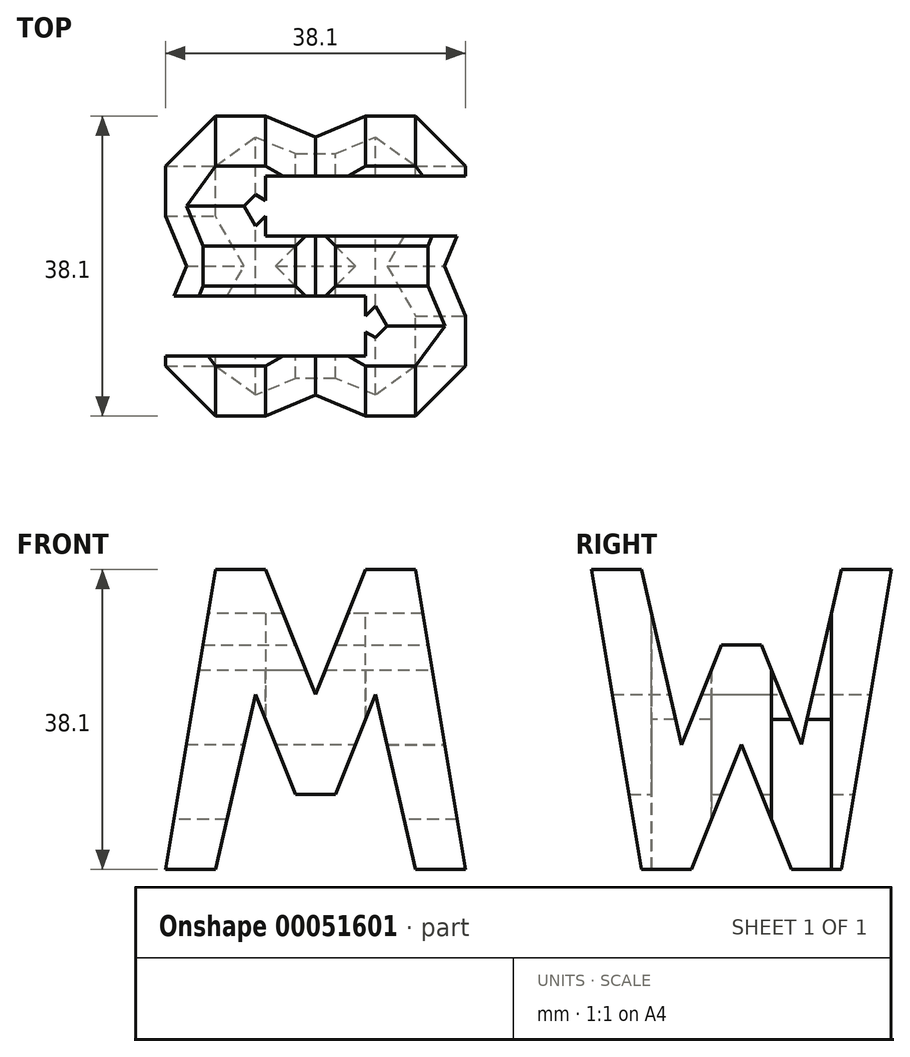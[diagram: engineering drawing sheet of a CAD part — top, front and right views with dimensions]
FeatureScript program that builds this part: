
annotation { "Feature Type Name" : "Feature", "Feature Type Description" : "" }
export const myFeature = defineFeature(function(context is Context, id is Id, definition is map)
    precondition{}
    {
        {
            var Q0;
            Q0=qCreatedBy(makeId("Front.planeOp"),FACE);
            var sketch = newSketch(context, id + "F0", { "sketchPlane" : qUnion([Q0])});
            skLineSegment(sketch, "E0.bottom", {"start": v(-38.1, 38.1) * mm, "end": v(0, 38.1) * mm});
            skLineSegment(sketch, "E0.top", {"start": v(-38.1, 0) * mm, "end": v(0, 0) * mm});
            skLineSegment(sketch, "E0.left", {"start": v(-38.1, 38.1) * mm, "end": v(-38.1, 0) * mm});
            skLineSegment(sketch, "E0.right", {"start": v(0, 38.1) * mm, "end": v(0, 0) * mm});
            skSolve(sketch);
        }
        {
            var Q0;
            Q0=makeQuery(id+"F0.imprint","IMPRINT",FACE,{"disambiguationData":[TD([[makeQuery(id+"F0.imprint","IMPRINT",EDGE,{"derivedFrom":sQuery(id+"F0.wireOp",EDGE,"E0.bottom")}),-1.0]])]});
            extrude(context, id + "F1", {"entities" : qUnion([Q0]), "depth" : 38.1 * mm});
        }
        {
            var Q0;
            Q0=qCreatedBy(makeId("Right.planeOp"),FACE);
            cPlane(context, id + "F2", {"entities" : qUnion([Q0]), "cplaneType" : CPlaneType.OFFSET, "offset" : 0 * mm, "width" : 152.4 * mm, "height" : 152.4 * mm});
        }
        {
            var Q0;
            Q0=qCreatedBy(makeId("Top.planeOp"),FACE);
            cPlane(context, id + "F3", {"entities" : qUnion([Q0]), "cplaneType" : CPlaneType.OFFSET, "offset" : 38.1 * mm, "width" : 152.4 * mm, "height" : 152.4 * mm});
        }
        {
            var Q0;
            Q0=qCreatedBy(id+"F2.planeOp",FACE);
            var sketch = newSketch(context, id + "F4", { "sketchPlane" : qUnion([Q0])});
            skLineSegment(sketch, "E1.bottom", {"start": v(0, 0) * mm, "end": v(-38.1, 0) * mm});
            skLineSegment(sketch, "E1.top", {"start": v(0, 38.1) * mm, "end": v(-38.1, 38.1) * mm});
            skLineSegment(sketch, "E1.left", {"start": v(0, 0) * mm, "end": v(0, 38.1) * mm});
            skLineSegment(sketch, "E1.right", {"start": v(-38.1, 0) * mm, "end": v(-38.1, 38.1) * mm});
            skLineSegment(sketch, "E2", {"start": v(-38.1, 38.1) * mm, "end": v(-31.75, 0) * mm});
            skLineSegment(sketch, "E3", {"start": v(-31.75, 0) * mm, "end": v(-25.4, 0) * mm});
            skLineSegment(sketch, "E4", {"start": v(-25.4, 0) * mm, "end": v(-19.05, 15.88) * mm});
            skLineSegment(sketch, "E5", {"start": v(-19.05, 15.88) * mm, "end": v(-12.7, 0) * mm});
            skLineSegment(sketch, "E6", {"start": v(-12.7, 0) * mm, "end": v(-6.35, 0) * mm});
            skLineSegment(sketch, "E7", {"start": v(-6.35, 0) * mm, "end": v(0, 38.1) * mm});
            skLineSegment(sketch, "E8", {"start": v(-6.35, 38.1) * mm, "end": v(-11.43, 15.87) * mm});
            skLineSegment(sketch, "E9", {"start": v(-21.6, 28.52) * mm, "end": v(-26.67, 15.82) * mm});
            skLineSegment(sketch, "E10", {"start": v(-26.67, 15.82) * mm, "end": v(-31.75, 38.1) * mm});
            skLineSegment(sketch, "E11", {"start": v(-31.75, 38.1) * mm, "end": v(-38.1, 38.1) * mm});
            skLineSegment(sketch, "E12", {"start": v(-21.6, 28.52) * mm, "end": v(-16.51, 28.52) * mm});
            skLineSegment(sketch, "E13", {"start": v(-11.43, 15.87) * mm, "end": v(-16.51, 28.52) * mm});
            skSolve(sketch);
        }
        {
            var Q0;
            {var subQ1=sQuery(id+"F4.wireOp",EDGE,"E8");Q0=makeQuery(id+"F4.imprint","IMPRINT",FACE,{"disambiguationData":[TD([[makeQuery(id+"F4.imprint","IMPRINT",EDGE,{"derivedFrom":subQ1}),-1.0]])]});}
            var Q1;
            {var subQ0=sQuery(id+"F4.wireOp",EDGE,"E1.right");Q1=makeQuery(id+"F4.imprint","IMPRINT",FACE,{"disambiguationData":[TD([[makeQuery(id+"F4.imprint","IMPRINT",EDGE,{"derivedFrom":subQ0}),-1.0]])]});}
            var Q2;
            {var subQ0=sQuery(id+"F4.wireOp",EDGE,"E4");Q2=makeQuery(id+"F4.imprint","IMPRINT",FACE,{"disambiguationData":[TD([[makeQuery(id+"F4.imprint","IMPRINT",EDGE,{"derivedFrom":subQ0}),-1.0]])]});}
            var Q3;
            {var subQ0=sQuery(id+"F4.wireOp",EDGE,"E1.left");Q3=makeQuery(id+"F4.imprint","IMPRINT",FACE,{"disambiguationData":[TD([[makeQuery(id+"F4.imprint","IMPRINT",EDGE,{"derivedFrom":subQ0}),1.0]])]});}
            extrude(context, id + "F5", {"entities" : qUnion([Q0, Q1, Q2, Q3]), "operationType" : NewBodyOperationType.REMOVE, "oppositeDirection" : true, "depth" : 38.1 * mm});
        }
        {
            var Q0;
            Q0=qCreatedBy(makeId("Front.planeOp"),FACE);
            var sketch = newSketch(context, id + "F6", { "sketchPlane" : qUnion([Q0])});
            skLineSegment(sketch, "E14", {"start": v(0, 38.1) * mm, "end": v(-38.1, 38.1) * mm});
            skLineSegment(sketch, "E15", {"start": v(-38.1, 38.1) * mm, "end": v(-38.1, 0) * mm});
            skLineSegment(sketch, "E16", {"start": v(-38.1, 0) * mm, "end": v(0, 0) * mm});
            skLineSegment(sketch, "E17", {"start": v(0, 0) * mm, "end": v(0, 38.1) * mm});
            skLineSegment(sketch, "E18", {"start": v(0, 0) * mm, "end": v(-6.35, 38.1) * mm});
            skLineSegment(sketch, "E19", {"start": v(-6.35, 38.1) * mm, "end": v(-12.7, 38.1) * mm});
            skLineSegment(sketch, "E20", {"start": v(-12.7, 38.1) * mm, "end": v(-19.05, 22.23) * mm});
            skLineSegment(sketch, "E21", {"start": v(-19.05, 22.23) * mm, "end": v(-25.4, 38.1) * mm});
            skLineSegment(sketch, "E22", {"start": v(-25.4, 38.1) * mm, "end": v(-31.75, 38.1) * mm});
            skLineSegment(sketch, "E23", {"start": v(-31.75, 38.1) * mm, "end": v(-38.1, 0) * mm});
            skLineSegment(sketch, "E24", {"start": v(-31.75, 0) * mm, "end": v(-26.67, 22.23) * mm});
            skLineSegment(sketch, "E25", {"start": v(-26.67, 22.23) * mm, "end": v(-21.6, 9.53) * mm});
            skLineSegment(sketch, "E26", {"start": v(-21.6, 9.53) * mm, "end": v(-16.51, 9.53) * mm});
            skLineSegment(sketch, "E27", {"start": v(-16.51, 9.52) * mm, "end": v(-11.43, 22.23) * mm});
            skLineSegment(sketch, "E28", {"start": v(-11.43, 22.23) * mm, "end": v(-6.35, 0) * mm});
            skLineSegment(sketch, "E29", {"start": v(-6.35, 0) * mm, "end": v(0, 0) * mm});
            skSolve(sketch);
        }
        {
            var Q0;
            {var subQ0=sQuery(id+"F6.wireOp",EDGE,"E17");Q0=makeQuery(id+"F6.imprint","IMPRINT",FACE,{"disambiguationData":[TD([[makeQuery(id+"F6.imprint","IMPRINT",EDGE,{"derivedFrom":subQ0}),1.0]])]});}
            var Q1;
            {var subQ0=sQuery(id+"F6.wireOp",EDGE,"E20");Q1=makeQuery(id+"F6.imprint","IMPRINT",FACE,{"disambiguationData":[TD([[makeQuery(id+"F6.imprint","IMPRINT",EDGE,{"derivedFrom":subQ0}),-1.0]])]});}
            var Q2;
            {var subQ0=sQuery(id+"F6.wireOp",EDGE,"E15");Q2=makeQuery(id+"F6.imprint","IMPRINT",FACE,{"disambiguationData":[TD([[makeQuery(id+"F6.imprint","IMPRINT",EDGE,{"derivedFrom":subQ0}),1.0]])]});}
            var Q3;
            {var subQ0=sQuery(id+"F6.wireOp",EDGE,"E24");Q3=makeQuery(id+"F6.imprint","IMPRINT",FACE,{"disambiguationData":[TD([[makeQuery(id+"F6.imprint","IMPRINT",EDGE,{"derivedFrom":subQ0}),-1.0]])]});}
            extrude(context, id + "F7", {"entities" : qUnion([Q0, Q1, Q2, Q3]), "operationType" : NewBodyOperationType.REMOVE, "depth" : 38.1 * mm});
        }
        {
            var Q0;
            Q0=qCreatedBy(id+"F3.planeOp",FACE);
            var sketch = newSketch(context, id + "F8", { "sketchPlane" : qUnion([Q0])});
            skLineSegment(sketch, "E30", {"start": v(0, 0) * mm, "end": v(-38.1, 0) * mm});
            skLineSegment(sketch, "E31", {"start": v(-38.1, 0) * mm, "end": v(-38.1, -38.1) * mm});
            skLineSegment(sketch, "E32", {"start": v(-38.1, -38.1) * mm, "end": v(0, -38.1) * mm});
            skLineSegment(sketch, "E33", {"start": v(0, -38.1) * mm, "end": v(0, 0) * mm});
            skLineSegment(sketch, "E34", {"start": v(0, -7.62) * mm, "end": v(-25.4, -7.62) * mm});
            skLineSegment(sketch, "E35", {"start": v(-25.4, -7.62) * mm, "end": v(-25.4, -15.24) * mm});
            skLineSegment(sketch, "E36", {"start": v(-25.4, -15.24) * mm, "end": v(0, -15.24) * mm});
            skLineSegment(sketch, "E37", {"start": v(-38.1, -22.86) * mm, "end": v(-12.7, -22.86) * mm});
            skLineSegment(sketch, "E38", {"start": v(-12.7, -22.86) * mm, "end": v(-12.7, -30.48) * mm});
            skLineSegment(sketch, "E39", {"start": v(-12.7, -30.48) * mm, "end": v(-38.1, -30.48) * mm});
            skSolve(sketch);
        }
        {
            var Q0;
            {var subQ0=sQuery(id+"F8.wireOp",EDGE,"E37");Q0=makeQuery(id+"F8.imprint","IMPRINT",FACE,{"disambiguationData":[TD([[makeQuery(id+"F8.imprint","IMPRINT",EDGE,{"derivedFrom":subQ0}),-1.0]])]});}
            var Q1;
            {var subQ0=sQuery(id+"F8.wireOp",EDGE,"E34");Q1=makeQuery(id+"F8.imprint","IMPRINT",FACE,{"disambiguationData":[TD([[makeQuery(id+"F8.imprint","IMPRINT",EDGE,{"derivedFrom":subQ0}),1.0]])]});}
            extrude(context, id + "F9", {"entities" : qUnion([Q0, Q1]), "operationType" : NewBodyOperationType.REMOVE, "oppositeDirection" : true, "depth" : 38.1 * mm});
        }
    });
